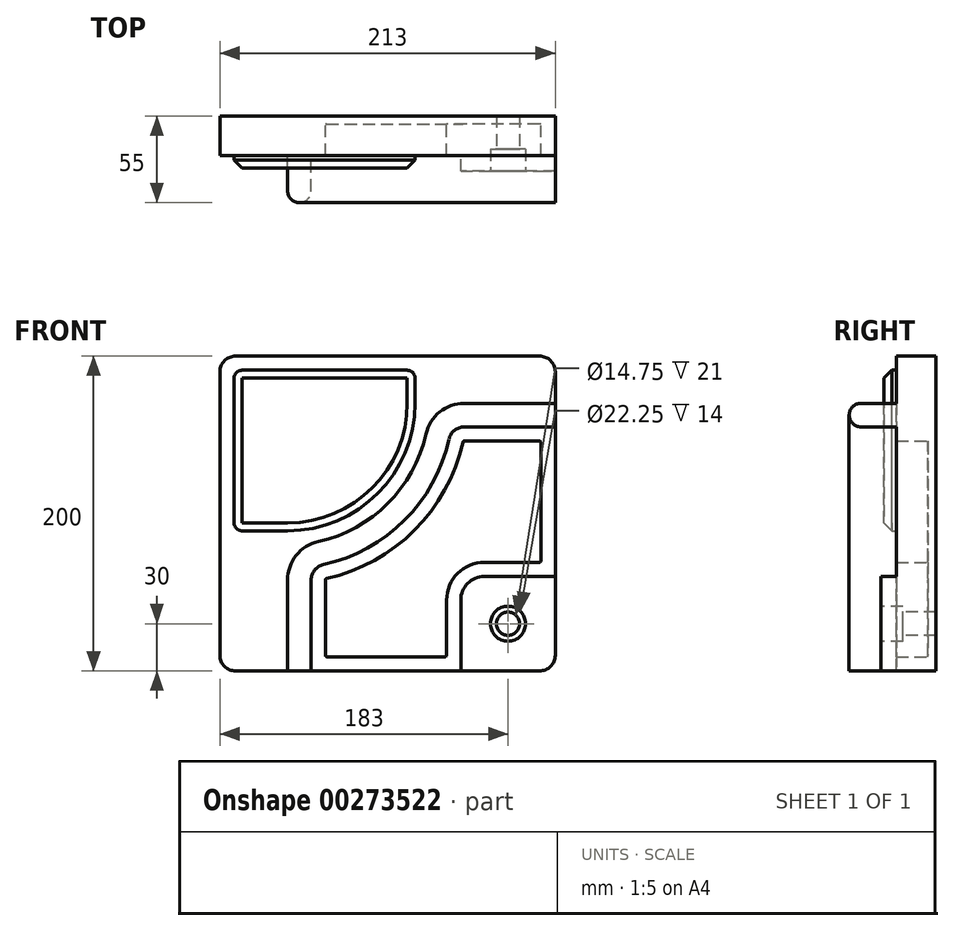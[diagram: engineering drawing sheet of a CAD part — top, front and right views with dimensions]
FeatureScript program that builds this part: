
annotation { "Feature Type Name" : "Feature", "Feature Type Description" : "" }
export const myFeature = defineFeature(function(context is Context, id is Id, definition is map)
    precondition{}
    {
        {
            var Q0;
            Q0=qCreatedBy(makeId("Front.planeOp"),FACE);
            var sketch = newSketch(context, id + "F0", { "sketchPlane" : qUnion([Q0])});
            skLineSegment(sketch, "E0.bottom", {"start": v(-96.5, -100) * mm, "end": v(96.5, -100) * mm});
            skLineSegment(sketch, "E0.top", {"start": v(-96.5, 100) * mm, "end": v(96.5, 100) * mm});
            skLineSegment(sketch, "E0.left", {"start": v(-106.5, -90) * mm, "end": v(-106.5, 90) * mm});
            skLineSegment(sketch, "E0.right", {"start": v(106.5, -90) * mm, "end": v(106.5, 90) * mm});
            skPoint(sketch, "E0.middle", {"position": v(0, 0) * mm});
            skPoint(sketch, "E1.visualSharp", {"position": v(106.5, 100) * mm});
            skArc(sketch, "E1.filletArc", {"start": v(106.5, 90) * mm, "mid": v(103.57, 97.07) * mm, "end": v(96.5, 100) * mm});
            skPoint(sketch, "E2.visualSharp", {"position": v(106.5, -100) * mm});
            skArc(sketch, "E2.filletArc", {"start": v(96.5, -100) * mm, "mid": v(103.57, -97.07) * mm, "end": v(106.5, -90) * mm});
            skPoint(sketch, "E3.visualSharp", {"position": v(-106.5, -100) * mm});
            skArc(sketch, "E3.filletArc", {"start": v(-106.5, -90) * mm, "mid": v(-103.57, -97.07) * mm, "end": v(-96.5, -100) * mm});
            skPoint(sketch, "E4.visualSharp", {"position": v(-106.5, 100) * mm});
            skArc(sketch, "E4.filletArc", {"start": v(-96.5, 100) * mm, "mid": v(-103.57, 97.07) * mm, "end": v(-106.5, 90) * mm});
            skLineSegment(sketch, "E5", {"start": v(-63.5, -100) * mm, "end": v(-63.5, -42.25) * mm});
            skLineSegment(sketch, "E6", {"start": v(106.5, 70) * mm, "end": v(48.75, 70) * mm});
            skPoint(sketch, "E7", {"position": v(76.5, -70) * mm});
            skLineSegment(sketch, "E8", {"start": v(106.5, -40) * mm, "end": v(61.5, -40) * mm});
            skLineSegment(sketch, "E9", {"start": v(46.5, -55) * mm, "end": v(46.5, -100) * mm});
            skPoint(sketch, "E10.visualSharp", {"position": v(46.5, -40) * mm});
            skArc(sketch, "E10.filletArc", {"start": v(61.5, -40) * mm, "mid": v(50.9, -44.4) * mm, "end": v(46.5, -55) * mm});
            skArc(sketch, "E11", {"start": v(-43.93, -17.85) * mm, "mid": v(-58, -26.61) * mm, "end": v(-63.5, -42.25) * mm});
            skArc(sketch, "E12", {"start": v(-43.93, -17.85) * mm, "mid": v(0.14, 6.36) * mm, "end": v(24.35, 50.43) * mm});
            skArc(sketch, "E13", {"start": v(48.75, 70) * mm, "mid": v(33.11, 64.5) * mm, "end": v(24.35, 50.43) * mm});
            skLineSegment(sketch, "E14.0", {"start": v(106.5, 55) * mm, "end": v(48.75, 55) * mm});
            skLineSegment(sketch, "E14.1", {"start": v(-48.5, -100) * mm, "end": v(-48.5, -42.25) * mm});
            skArc(sketch, "E14.2", {"start": v(-40.67, -32.49) * mm, "mid": v(-46.3, -36) * mm, "end": v(-48.5, -42.25) * mm});
            skArc(sketch, "E14.3", {"start": v(-40.67, -32.49) * mm, "mid": v(10.75, -4.25) * mm, "end": v(38.99, 47.17) * mm});
            skArc(sketch, "E14.4", {"start": v(48.75, 55) * mm, "mid": v(42.5, 52.8) * mm, "end": v(38.99, 47.17) * mm});
            skLineSegment(sketch, "E15.bottom", {"start": v(-92.5, 91) * mm, "end": v(12.5, 91) * mm});
            skLineSegment(sketch, "E15.top", {"start": v(-92.5, -11) * mm, "end": v(-63.5, -11) * mm});
            skLineSegment(sketch, "E15.left", {"start": v(-97.5, 86) * mm, "end": v(-97.5, -6) * mm});
            skLineSegment(sketch, "E15.right", {"start": v(17.5, 86) * mm, "end": v(17.5, 70) * mm});
            skPoint(sketch, "E16.visualSharp", {"position": v(17.5, -11) * mm});
            skArc(sketch, "E16.filletArc", {"start": v(-63.5, -11) * mm, "mid": v(-6.22, 12.72) * mm, "end": v(17.5, 70) * mm});
            skPoint(sketch, "E17.visualSharp", {"position": v(-97.5, 91) * mm});
            skArc(sketch, "E17.filletArc", {"start": v(-92.5, 91) * mm, "mid": v(-96.04, 89.54) * mm, "end": v(-97.5, 86) * mm});
            skPoint(sketch, "E18.visualSharp", {"position": v(17.5, 91) * mm});
            skArc(sketch, "E18.filletArc", {"start": v(17.5, 86) * mm, "mid": v(16.04, 89.54) * mm, "end": v(12.5, 91) * mm});
            skPoint(sketch, "E19.visualSharp", {"position": v(-97.5, -11) * mm});
            skArc(sketch, "E19.filletArc", {"start": v(-97.5, -6) * mm, "mid": v(-96.04, -9.54) * mm, "end": v(-92.5, -11) * mm});
            skLineSegment(sketch, "E20.0", {"start": v(96.5, 46) * mm, "end": v(48.75, 46) * mm});
            skLineSegment(sketch, "E20.1", {"start": v(-39.5, -90) * mm, "end": v(-39.5, -42.25) * mm});
            skArc(sketch, "E20.2", {"start": v(-38.72, -41.27) * mm, "mid": v(-39.28, -41.62) * mm, "end": v(-39.5, -42.25) * mm});
            skArc(sketch, "E20.3", {"start": v(-38.72, -41.27) * mm, "mid": v(17.11, -10.61) * mm, "end": v(47.77, 45.22) * mm});
            skArc(sketch, "E20.4", {"start": v(48.75, 46) * mm, "mid": v(48.12, 45.78) * mm, "end": v(47.77, 45.22) * mm});
            skLineSegment(sketch, "E21.0", {"start": v(37.5, -55) * mm, "end": v(37.5, -90) * mm});
            skArc(sketch, "E21.1", {"start": v(61.5, -31) * mm, "mid": v(44.53, -38.03) * mm, "end": v(37.5, -55) * mm});
            skLineSegment(sketch, "E21.2", {"start": v(96.5, -31) * mm, "end": v(61.5, -31) * mm});
            skLineSegment(sketch, "E22", {"start": v(-38.5, -91) * mm, "end": v(36.5, -91) * mm});
            skLineSegment(sketch, "E23", {"start": v(97.5, 45) * mm, "end": v(97.5, -30) * mm});
            skPoint(sketch, "E24.visualSharp", {"position": v(97.5, 46) * mm});
            skArc(sketch, "E24.filletArc", {"start": v(97.5, 45) * mm, "mid": v(97.2, 45.7) * mm, "end": v(96.5, 46) * mm});
            skPoint(sketch, "E25.visualSharp", {"position": v(97.5, -31) * mm});
            skArc(sketch, "E25.filletArc", {"start": v(96.5, -31) * mm, "mid": v(97.2, -30.7) * mm, "end": v(97.5, -30) * mm});
            skPoint(sketch, "E26.visualSharp", {"position": v(37.5, -91) * mm});
            skArc(sketch, "E26.filletArc", {"start": v(36.5, -91) * mm, "mid": v(37.2, -90.7) * mm, "end": v(37.5, -90) * mm});
            skPoint(sketch, "E27.visualSharp", {"position": v(-39.5, -91) * mm});
            skArc(sketch, "E27.filletArc", {"start": v(-39.5, -90) * mm, "mid": v(-39.2, -90.7) * mm, "end": v(-38.5, -91) * mm});
            skSolve(sketch);
        }
        {
            var Q0;
            Q0 = qSketchRegion(id + "F0", true);
            extrude(context, id + "F1", {"entities" : qUnion([Q0]), "depth" : 25 * mm});
        }
        {
            var Q0;
            {var subQ0=sQuery(id+"F0.wireOp",EDGE,"E2.filletArc");Q0=makeQuery(id+"F0.imprint","IMPRINT",FACE,{"disambiguationData":[TD([[makeQuery(id+"F0.imprint","IMPRINT",EDGE,{"derivedFrom":subQ0}),1.0]])]});}
            extrude(context, id + "F2", {"entities" : qUnion([Q0]), "operationType" : NewBodyOperationType.ADD, "depth" : 35 * mm});
        }
        {
            var Q0;
            Q0=makeQuery(id+"F2.opExtrude","CAP_FACE",FACE,{"disambiguationData":[OSD([sQuery(id+"F0.wireOp",EDGE,"E0.bottom"),sQuery(id+"F0.wireOp",EDGE,"E0.right"),sQuery(id+"F0.wireOp",EDGE,"E2.filletArc"),sQuery(id+"F0.wireOp",EDGE,"E8"),sQuery(id+"F0.wireOp",EDGE,"E9"),sQuery(id+"F0.wireOp",EDGE,"E10.filletArc")])],"isStart":false});
            var sketch = newSketch(context, id + "F3", { "sketchPlane" : qUnion([Q0])});
            skPoint(sketch, "E28", {"position": v(76.5, -70) * mm});
            skSolve(sketch);
        }
        {
            var Q0;
            Q0=sQuery(id+"F3.wireOp",VERTEX,"E28");
            var Q1;
            Q1=makeQuery(id+"F1.opExtrude","SWEPT_BODY",BODY,{"disambiguationData":[OSD([sQuery(id+"F0.wireOp",EDGE,"E0.bottom"),sQuery(id+"F0.wireOp",EDGE,"E0.top"),sQuery(id+"F0.wireOp",EDGE,"E0.left"),sQuery(id+"F0.wireOp",EDGE,"E0.right"),sQuery(id+"F0.wireOp",EDGE,"E1.filletArc"),sQuery(id+"F0.wireOp",EDGE,"E2.filletArc"),sQuery(id+"F0.wireOp",EDGE,"E3.filletArc"),sQuery(id+"F0.wireOp",EDGE,"E4.filletArc"),sQuery(id+"F0.wireOp",EDGE,"E15.bottom"),sQuery(id+"F0.wireOp",EDGE,"E15.top"),sQuery(id+"F0.wireOp",EDGE,"E15.left"),sQuery(id+"F0.wireOp",EDGE,"E15.right"),sQuery(id+"F0.wireOp",EDGE,"E16.filletArc"),sQuery(id+"F0.wireOp",EDGE,"E17.filletArc"),sQuery(id+"F0.wireOp",EDGE,"E18.filletArc"),sQuery(id+"F0.wireOp",EDGE,"E19.filletArc"),sQuery(id+"F0.wireOp",EDGE,"E20.0"),sQuery(id+"F0.wireOp",EDGE,"E20.1"),sQuery(id+"F0.wireOp",EDGE,"E20.2"),sQuery(id+"F0.wireOp",EDGE,"E20.3"),sQuery(id+"F0.wireOp",EDGE,"E20.4"),sQuery(id+"F0.wireOp",EDGE,"E21.0"),sQuery(id+"F0.wireOp",EDGE,"E21.1"),sQuery(id+"F0.wireOp",EDGE,"E21.2"),sQuery(id+"F0.wireOp",EDGE,"E22"),sQuery(id+"F0.wireOp",EDGE,"E23"),sQuery(id+"F0.wireOp",EDGE,"E24.filletArc"),sQuery(id+"F0.wireOp",EDGE,"E25.filletArc"),sQuery(id+"F0.wireOp",EDGE,"E26.filletArc"),sQuery(id+"F0.wireOp",EDGE,"E27.filletArc")])]});
            hole(context, id + "F4", {"style" : HoleStyle.C_BORE, "endStyle" : HoleEndStyle.THROUGH, "standardTappedOrClearance" : lookupTablePath({ "standard" : "ISO", "fit" : "Close", "size" : "M14", "type" : "Clearance" }), "standardBlindInLast" : lookupTablePath({ "fit" : "Close", "standard" : "ISO", "size" : "M14", "type" : "Clearance" }), "holeDiameter" : 14.75 * mm, "cBoreDiameter" : 22.25 * mm, "cBoreDepth" : 14 * mm, "tappedDepth" : 12 * mm, "tapClearance" : 3, "locations" : qUnion([Q0]), "scope" : qUnion([Q1])});
        }
        {
            var Q0;
            {var subQ4=sQuery(id+"F0.wireOp",EDGE,"E5");Q0=makeQuery(id+"F0.imprint","IMPRINT",FACE,{"disambiguationData":[TD([[makeQuery(id+"F0.imprint","IMPRINT",EDGE,{"derivedFrom":subQ4}),-1.0]])]});}
            extrude(context, id + "F5", {"entities" : qUnion([Q0]), "operationType" : NewBodyOperationType.ADD, "depth" : 55 * mm});
        }
        {
            var Q0;
            Q0=makeQuery(id+"F5.opExtrude","CAP_EDGE",EDGE,{"disambiguationData":[OSD([sQuery(id+"F0.wireOp",EDGE,"E14.1")])],"isStart":false});
            var Q1;
            Q1=makeQuery(id+"F5.opExtrude","CAP_EDGE",EDGE,{"disambiguationData":[OSD([sQuery(id+"F0.wireOp",EDGE,"E5")])],"isStart":false});
            fillet(context, id + "F6", {"entities" : qUnion([Q0, Q1]), "radius" : 7.5 * mm, "tangentPropagation" : true, "allowEdgeOverflow" : false});
        }
        {
            var Q0;
            Q0=makeQuery(id+"F0.imprint","IMPRINT",FACE,{"disambiguationData":[TD([[makeQuery(id+"F0.imprint","IMPRINT",EDGE,{"derivedFrom":sQuery(id+"F0.wireOp",EDGE,"E20.0")}),1.0]])]});
            extrude(context, id + "F7", {"entities" : qUnion([Q0]), "operationType" : NewBodyOperationType.ADD, "depth" : 5 * mm});
        }
        {
            var Q0;
            Q0=makeQuery(id+"F0.imprint","IMPRINT",FACE,{"disambiguationData":[TD([[makeQuery(id+"F0.imprint","IMPRINT",EDGE,{"derivedFrom":sQuery(id+"F0.wireOp",EDGE,"E15.bottom")}),-1.0]])]});
            extrude(context, id + "F8", {"entities" : qUnion([Q0]), "operationType" : NewBodyOperationType.ADD, "depth" : 33 * mm});
        }
        {
            var Q0;
            Q0=makeQuery(id+"F8.opExtrude","CAP_EDGE",EDGE,{"disambiguationData":[OSD([sQuery(id+"F0.wireOp",EDGE,"E15.bottom")])],"isStart":false});
            chamfer(context, id + "F9", {"entities" : qUnion([Q0]), "chamferType" : ChamferType.OFFSET_ANGLE, "width" : 5 * mm, "oppositeDirection" : false, "angle" : 45 * degree, "tangentPropagation" : true});
        }
    });
